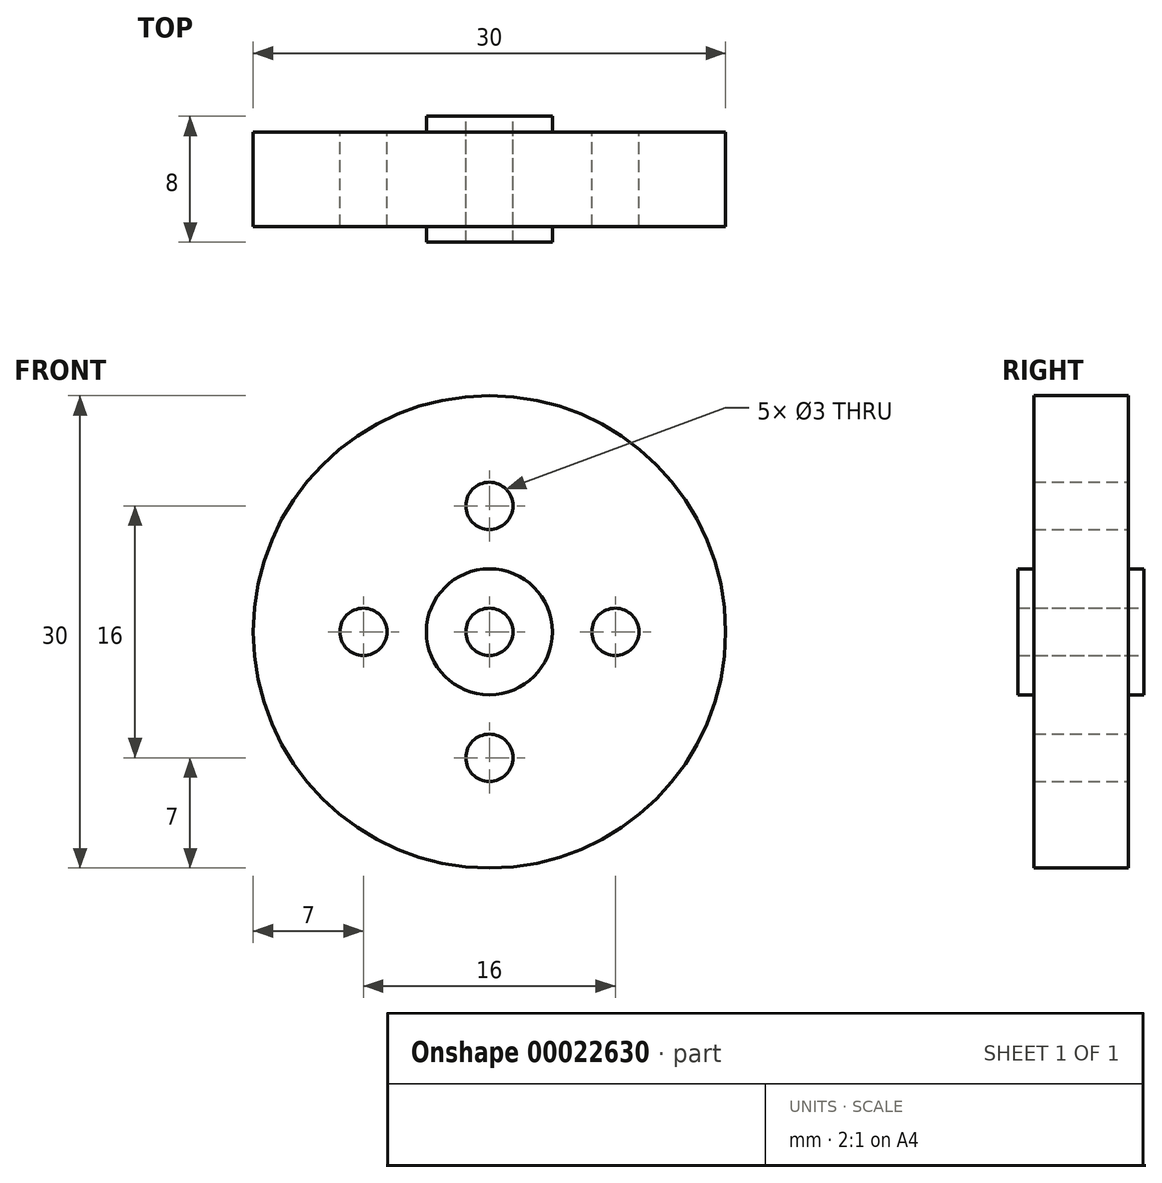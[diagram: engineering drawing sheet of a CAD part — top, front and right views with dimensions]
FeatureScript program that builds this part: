
annotation { "Feature Type Name" : "Feature", "Feature Type Description" : "" }
export const myFeature = defineFeature(function(context is Context, id is Id, definition is map)
    precondition{}
    {
        {
            var Q0;
            Q0=qCreatedBy(makeId("Front.planeOp"),FACE);
            var sketch = newSketch(context, id + "F0", { "sketchPlane" : qUnion([Q0])});
            skCircle(sketch, "E0", {"center": v(0, 0) * mm, "radius": 15 * mm});
            skCircle(sketch, "E1", {"center": v(0, 0) * mm, "radius": 1.5 * mm});
            skCircle(sketch, "E2", {"center": v(0, 8) * mm, "radius": 1.5 * mm});
            skCircle(sketch, "E3.1.0", {"center": v(-8, 0) * mm, "radius": 1.5 * mm});
            skCircle(sketch, "E3.2.0", {"center": v(0, -8) * mm, "radius": 1.5 * mm});
            skCircle(sketch, "E3.3.0", {"center": v(8, 0) * mm, "radius": 1.5 * mm});
            skSolve(sketch);
        }
        {
            var Q0;
            Q0=makeQuery(id+"F0.imprint","IMPRINT",FACE,{"disambiguationData":[TD([[makeQuery(id+"F0.imprint","IMPRINT",EDGE,{"derivedFrom":sQuery(id+"F0.wireOp",EDGE,"E0")}),1.0]])]});
            extrude(context, id + "F1", {"entities" : qUnion([Q0]), "depth" : 6 * mm});
        }
        {
            var Q0;
            Q0=makeQuery(id+"F1.opExtrude","CAP_FACE",FACE,{"disambiguationData":[OSD([sQuery(id+"F0.wireOp",EDGE,"E0"),sQuery(id+"F0.wireOp",EDGE,"E1"),sQuery(id+"F0.wireOp",EDGE,"E2"),sQuery(id+"F0.wireOp",EDGE,"E3.1.0"),sQuery(id+"F0.wireOp",EDGE,"E3.2.0"),sQuery(id+"F0.wireOp",EDGE,"E3.3.0")])],"isStart":false});
            var sketch = newSketch(context, id + "F2", { "sketchPlane" : qUnion([Q0])});
            skCircle(sketch, "E4", {"center": v(0, 0) * mm, "radius": 4 * mm});
            skSolve(sketch);
        }
        {
            var Q0;
            Q0=makeQuery(id+"F2.imprint","IMPRINT",FACE,{"disambiguationData":[TD([[makeQuery(id+"F2.imprint","IMPRINT",EDGE,{"derivedFrom":makeQuery(id+"F1.opExtrude","CAP_EDGE",EDGE,{"disambiguationData":[OSD([sQuery(id+"F0.wireOp",EDGE,"E1")])],"isStart":false})}),1.0]])]});
            var Q1;
            Q1=makeQuery(id+"F2.imprint","IMPRINT",FACE,{"disambiguationData":[TD([[makeQuery(id+"F2.imprint","IMPRINT",EDGE,{"derivedFrom":sQuery(id+"F2.wireOp",EDGE,"E4")}),1.0]])]});
            extrude(context, id + "F3", {"entities" : qUnion([Q0, Q1]), "operationType" : NewBodyOperationType.ADD, "depth" : 1 * mm});
        }
        {
            var Q0;
            Q0=makeQuery(id+"F1.opExtrude","CAP_FACE",FACE,{"disambiguationData":[OSD([sQuery(id+"F0.wireOp",EDGE,"E0"),sQuery(id+"F0.wireOp",EDGE,"E1"),sQuery(id+"F0.wireOp",EDGE,"E2"),sQuery(id+"F0.wireOp",EDGE,"E3.1.0"),sQuery(id+"F0.wireOp",EDGE,"E3.2.0"),sQuery(id+"F0.wireOp",EDGE,"E3.3.0")])],"isStart":true});
            var sketch = newSketch(context, id + "F4", { "sketchPlane" : qUnion([Q0])});
            skCircle(sketch, "E5", {"center": v(0, 0) * mm, "radius": 4 * mm});
            skSolve(sketch);
        }
        {
            var Q0;
            Q0=makeQuery(id+"F4.imprint","IMPRINT",FACE,{"disambiguationData":[TD([[makeQuery(id+"F4.imprint","IMPRINT",EDGE,{"derivedFrom":makeQuery(id+"F1.opExtrude","CAP_EDGE",EDGE,{"disambiguationData":[OSD([sQuery(id+"F0.wireOp",EDGE,"E1")])],"isStart":true})}),-1.0]])]});
            var Q1;
            Q1=makeQuery(id+"F4.imprint","IMPRINT",FACE,{"disambiguationData":[TD([[makeQuery(id+"F4.imprint","IMPRINT",EDGE,{"derivedFrom":sQuery(id+"F4.wireOp",EDGE,"E5")}),1.0]])]});
            extrude(context, id + "F5", {"entities" : qUnion([Q0, Q1]), "operationType" : NewBodyOperationType.ADD, "depth" : 1 * mm});
        }
        {
            var Q0;
            Q0=makeQuery(id+"F5.opExtrude","CAP_FACE",FACE,{"disambiguationData":[OSD([sQuery(id+"F4.wireOp",EDGE,"E5")])],"isStart":false});
            var sketch = newSketch(context, id + "F6", { "sketchPlane" : qUnion([Q0])});
            skCircle(sketch, "E6", {"center": v(0, 0) * mm, "radius": 1.5 * mm});
            skSolve(sketch);
        }
        {
            var Q0;
            Q0=makeQuery(id+"F6.imprint","IMPRINT",FACE,{"disambiguationData":[TD([[makeQuery(id+"F6.imprint","IMPRINT",EDGE,{"derivedFrom":sQuery(id+"F6.wireOp",EDGE,"E6")}),1.0]])]});
            extrude(context, id + "F7", {"entities" : qUnion([Q0]), "operationType" : NewBodyOperationType.REMOVE, "oppositeDirection" : true, "depth" : 25.4 * mm});
        }
    });
